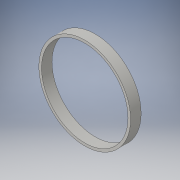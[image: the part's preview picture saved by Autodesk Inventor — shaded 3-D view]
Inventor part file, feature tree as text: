
AUTODESK INVENTOR PART (.ipt)
format: ipt  version: 2016 (Build 200138000, 138)  size: 99,328 bytes
history: native  units: in
note: dims shown in document units (in); Inventor stores cm internally (conversion verified against a paired STEP export)
features: extrude x1, shell x1, sketch x1
ambient origin geometry x8: Origin, YZ Plane, XZ Plane, XY Plane, X Axis, Y Axis, Z Axis, Center Point
bodies: Solid1 (feature_tree)
feature tree (3):
  extrude  "Extrusion1"  Depth=0.4in TaperAngle=0.0deg
  shell  "Shell1"  Thickness=0.1in
  sketch  "Sketch1"  dims[d0=3.5in d1=0.4in d2=0.0in d3=0.1in]
